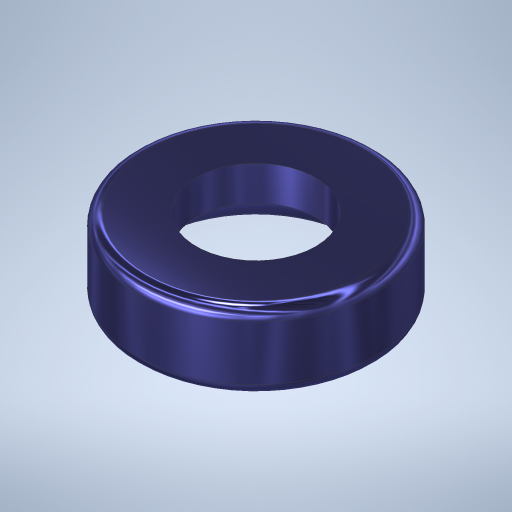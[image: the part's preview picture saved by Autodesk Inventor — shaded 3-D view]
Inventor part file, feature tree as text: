
AUTODESK INVENTOR PART (.ipt)
format: ipt  version: 2023.1 (Build 271208000, 208)  size: 316,416 bytes
history: native  units: in
note: dims shown in document units (in); Inventor stores cm internally (conversion verified against a paired STEP export)
features: sketch x2, revolve x1, fillet x1, extrude x1
ambient origin geometry x8: Origin, YZ Plane, XZ Plane, XY Plane, X Axis, Y Axis, Z Axis, Center Point
bodies: Solid1 (feature_tree)
feature tree (5):
  revolve  "Revolution1"  [1 undecoded]
  fillet  "Fillet1"  Radius=0.025in
  extrude  "Extrusion1"  TaperAngle=90.0deg  [1 undecoded]
  sketch  "Sketch1"  dims[d0=0.1875in d1=0.1625in d2=0.025in]
  sketch  "Sketch2"  dims[d3=0.1625in d4=90.0deg d5=0.015in d6=0.1625in d7=0.0in d8=0.0in]
note: 2 required parameter values undecoded (feature->parameter linkage not recoverable at this tier; creation-order binding heuristic only, values carry confidence <= 0.55)